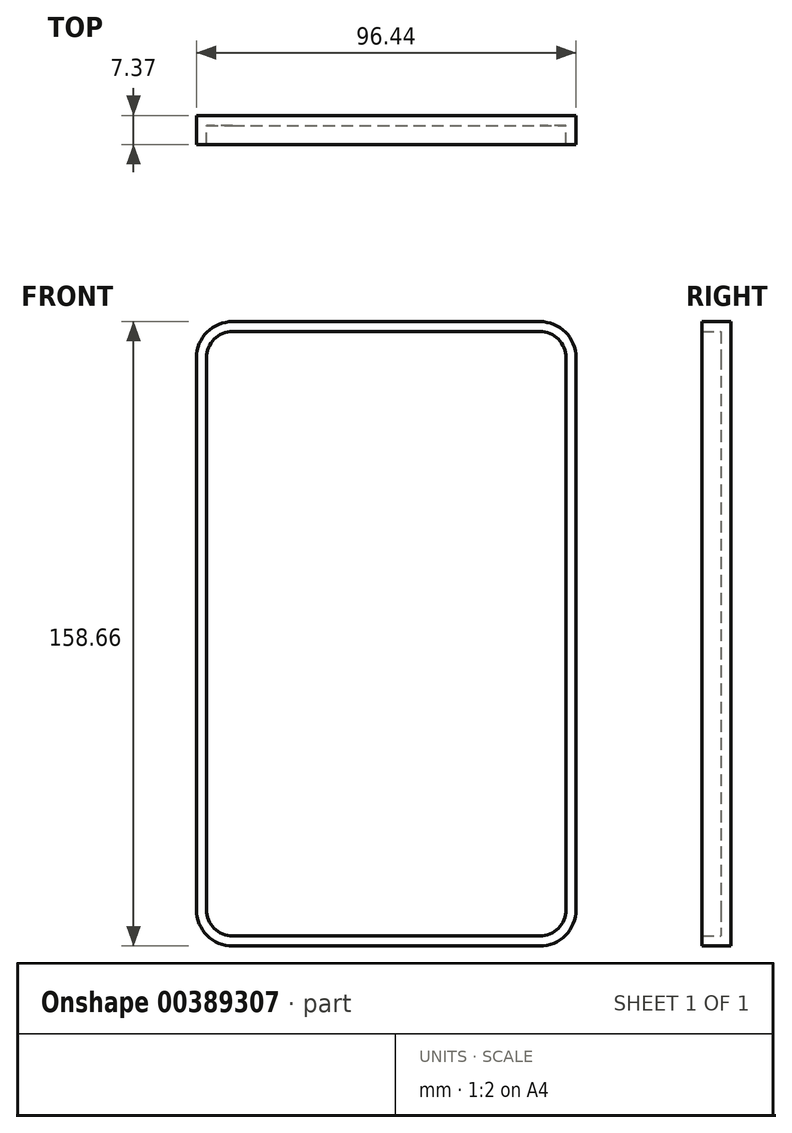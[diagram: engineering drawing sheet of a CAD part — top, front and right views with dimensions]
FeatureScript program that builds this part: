
annotation { "Feature Type Name" : "Feature", "Feature Type Description" : "" }
export const myFeature = defineFeature(function(context is Context, id is Id, definition is map)
    precondition{}
    {
        {
            var Q0;
            Q0=qCreatedBy(makeId("Front.planeOp"),FACE);
            var sketch = newSketch(context, id + "F0", { "sketchPlane" : qUnion([Q0])});
            skLineSegment(sketch, "E0.bottom", {"start": v(-49.56, 85.55) * mm, "end": v(28.48, 85.55) * mm});
            skLineSegment(sketch, "E0.top", {"start": v(-49.56, -73.1) * mm, "end": v(28.48, -73.1) * mm});
            skLineSegment(sketch, "E0.left", {"start": v(-58.76, 76.35) * mm, "end": v(-58.76, -63.91) * mm});
            skLineSegment(sketch, "E0.right", {"start": v(37.68, 76.35) * mm, "end": v(37.68, -63.91) * mm});
            skPoint(sketch, "E1.visualSharp", {"position": v(-58.76, 85.55) * mm});
            skArc(sketch, "E1.filletArc", {"start": v(-49.56, 85.55) * mm, "mid": v(-56.06, 82.85) * mm, "end": v(-58.76, 76.35) * mm});
            skPoint(sketch, "E2.visualSharp", {"position": v(37.68, 85.55) * mm});
            skArc(sketch, "E2.filletArc", {"start": v(37.68, 76.35) * mm, "mid": v(34.99, 82.85) * mm, "end": v(28.48, 85.55) * mm});
            skPoint(sketch, "E3.visualSharp", {"position": v(-58.76, -73.1) * mm});
            skArc(sketch, "E3.filletArc", {"start": v(-58.76, -63.91) * mm, "mid": v(-56.06, -70.41) * mm, "end": v(-49.56, -73.1) * mm});
            skPoint(sketch, "E4.visualSharp", {"position": v(37.68, -73.1) * mm});
            skArc(sketch, "E4.filletArc", {"start": v(28.48, -73.1) * mm, "mid": v(34.99, -70.41) * mm, "end": v(37.68, -63.91) * mm});
            skSolve(sketch);
        }
        {
            var Q0;
            Q0=makeQuery(id+"F0.imprint","IMPRINT",FACE,{"disambiguationData":[TD([[makeQuery(id+"F0.imprint","IMPRINT",EDGE,{"derivedFrom":sQuery(id+"F0.wireOp",EDGE,"E0.bottom")}),-1.0]])]});
            extrude(context, id + "F1", {"entities" : qUnion([Q0]), "depth" : 7.37 * mm});
        }
        {
            var Q0;
            Q0=makeQuery(id+"F1.opExtrude","CAP_FACE",FACE,{"disambiguationData":[OSD([sQuery(id+"F0.wireOp",EDGE,"E0.bottom"),sQuery(id+"F0.wireOp",EDGE,"E0.top"),sQuery(id+"F0.wireOp",EDGE,"E0.left"),sQuery(id+"F0.wireOp",EDGE,"E0.right"),sQuery(id+"F0.wireOp",EDGE,"E1.filletArc"),sQuery(id+"F0.wireOp",EDGE,"E2.filletArc"),sQuery(id+"F0.wireOp",EDGE,"E3.filletArc"),sQuery(id+"F0.wireOp",EDGE,"E4.filletArc")])],"isStart":false});
            shell(context, id + "F2", {"entities" : qUnion([Q0]), "thickness" : 2.54 * mm});
        }
    });
